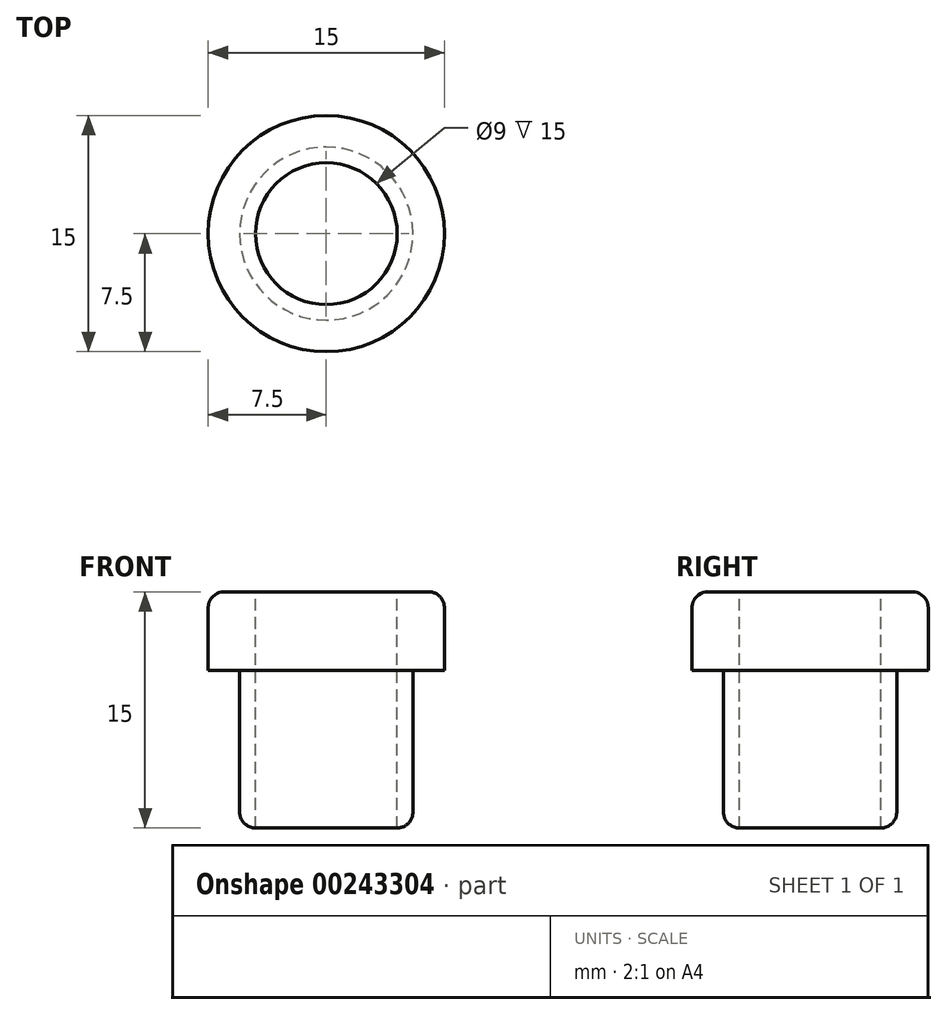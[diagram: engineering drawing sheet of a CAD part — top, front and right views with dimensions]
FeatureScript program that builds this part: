
annotation { "Feature Type Name" : "Feature", "Feature Type Description" : "" }
export const myFeature = defineFeature(function(context is Context, id is Id, definition is map)
    precondition{}
    {
        {
            var Q0;
            Q0=qCreatedBy(makeId("Top.planeOp"),FACE);
            var sketch = newSketch(context, id + "F0", { "sketchPlane" : qUnion([Q0])});
            skCircle(sketch, "E0", {"center": v(0, 0) * mm, "radius": 5.5 * mm});
            skCircle(sketch, "E1", {"center": v(0, 0) * mm, "radius": 4.5 * mm});
            skCircle(sketch, "E2", {"center": v(0, 0) * mm, "radius": 7.5 * mm});
            skSolve(sketch);
        }
        {
            var Q0;
            Q0=makeQuery(id+"F0.imprint","IMPRINT",FACE,{"disambiguationData":[TD([[makeQuery(id+"F0.imprint","IMPRINT",EDGE,{"derivedFrom":sQuery(id+"F0.wireOp",EDGE,"E0")}),1.0]])]});
            extrude(context, id + "F1", {"entities" : qUnion([Q0]), "oppositeDirection" : true, "depth" : 15 * mm});
        }
        {
            var Q0;
            Q0=makeQuery(id+"F0.imprint","IMPRINT",FACE,{"disambiguationData":[TD([[makeQuery(id+"F0.imprint","IMPRINT",EDGE,{"derivedFrom":sQuery(id+"F0.wireOp",EDGE,"E0")}),-1.0]])]});
            extrude(context, id + "F2", {"entities" : qUnion([Q0]), "operationType" : NewBodyOperationType.ADD, "oppositeDirection" : true, "depth" : 5 * mm});
        }
        {
            var Q0;
            Q0=makeQuery(id+"F2.opExtrude","CAP_EDGE",EDGE,{"disambiguationData":[OSD([sQuery(id+"F0.wireOp",EDGE,"E2")])],"isStart":true});
            var Q1;
            Q1=makeQuery(id+"F1.opExtrude","CAP_EDGE",EDGE,{"disambiguationData":[OSD([sQuery(id+"F0.wireOp",EDGE,"E0")])],"isStart":false});
            fillet(context, id + "F3", {"entities" : qUnion([Q0, Q1]), "radius" : 1 * mm, "tangentPropagation" : true, "allowEdgeOverflow" : false});
        }
    });
